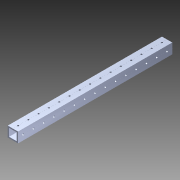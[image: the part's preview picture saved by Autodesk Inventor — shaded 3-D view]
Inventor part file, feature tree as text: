
AUTODESK INVENTOR PART (.ipt)
format: ipt  version: 2014 SP1 (Build 180222100, 222)  size: 1,181,696 bytes
history: native  units: in
note: dims shown in document units (in); Inventor stores cm internally (conversion verified against a paired STEP export)
features: pattern_circular x1, other x1, plane x1, extrude x1, imported_body x1, sketch x1
ambient origin geometry x8: Origin, YZ Plane, XZ Plane, XY Plane, X Axis, Y Axis, Z Axis, Center Point
bodies: Body1 (feature_tree)
feature tree (6):
  pattern_circular  "CirPattern2"
  other  "217-3426-STEP1"
  plane  "Work Plane1"
  extrude  "Extrusion1"  Depth=3937.0079in TaperAngle=0.0deg
  imported_body  "Base1"
  sketch  "Sketch1"  dims[d0=-15.0in d1=3937.0079in d2=0.0in]
